SOLIDWORKS PART (.sldprt)
format: sldprt  version: not decoded by parser v0  size: 265,216 bytes
history: native  units: mm
features: sketch x5, plane x4, cut_revolve x4, material x1, revolve x1, thread x1, cut_extrude x1, pattern_circular x1, pattern_linear x1 (+10 scaffold rows collapsed)
feature tree (29):
  scaffold x10  (default folders/planes/origin — collapsed)
  material  "Material <sin especificar>"
  plane  "Plane1"
  plane  "Plane2"
  plane  "Plane3"
  sketch  "BodySke"  dims[D1=~7.099516mm Head_ang=85.0deg Oval_ht=0.3048mm Head_ht=0.8128mm Diameter=1.524mm Length=30.48mm Head_dia=3.2004mm Advance=0.3175mm Thread_nom=7.62mm Thread_lim=36.5125mm]
  revolve  "Base-Revolve"  [1 undecoded]
  thread  "ThreadCosmetic"  Diameter=7.62mm Thread_length=7.62mm Thread_minor=1.14554mm  [1 undecoded]
  sketch  "Sketch2"  dims[D1=3.2004mm D2=1.6002mm D3=0.2921mm Slot_width=0.5842mm]
  cut_extrude  "Slot"  Depth=0.4572mm Slot_depth=0.4572mm
  sketch  "Sketch3"  dims[Cross_width=0.5842mm D1=0.2921mm Cross_dia=2.1082mm D2=1.0541mm]
  plane  "Plane4"  Offset=1.0668mm Cross_depth=1.0668mm
  sketch  "Sketch4"  dims[D1=0.2921mm D2=~0.14605mm D3=0.2921mm D4=~0.14605mm]
  pattern_circular  "CirPattern1"  Count=2 Angle=90deg
  sketch  "ThdSchSke"  dims[c1.Thread_minor=~1.03886mm c1.Diameter=~1.413535mm c1.Start=~0.988134mm c1.D4=~4.446753mm c1.Vee=60.0deg c2.Thread_minor=~1.03886mm c2.Start=~2.540025mm c2.D1=~0.108159mm c2.D2=~0.108159mm c3.D1=~0.216319mm c3.SideAngle=55.0deg c3.D2=~0.216319mm c3.VeeAngle=70.0deg c3.Thread_minor=~1.14554mm c3.Overcut=1.905mm c3.Diameter=1.524mm c3.D6=~8.326268mm c4.D1=~8.326268mm c5.D1=90.0deg c5.Start=11.1125mm c6.Start=~44.450025mm c7.Start=23.6728mm]
  cut_revolve  "ThreadSchematic"  Angle=360deg
  pattern_linear  "ThdSchPat"  Count1=25 Count2=1 Spacing1=0.3175mm Spacing2=50mm Num_threads=25 Advance=0.3175mm
  cut_revolve  "ConfigurationName"  CopiedFlag=0  [1 undecoded]
  cut_revolve  "PartNumberID"  [1 undecoded]
  cut_revolve  "ConfigurationName"  CopiedFlag=0  [1 undecoded]
decode coverage: 12 of 14 modeling features carry decoded parameters
note: ~ marks probable driven/reference dimensions
note: 5 parameter values undecoded
summary: no parameter record found for 4 features
note: suppression state not decoded; provenance and decode notes live in map.json
